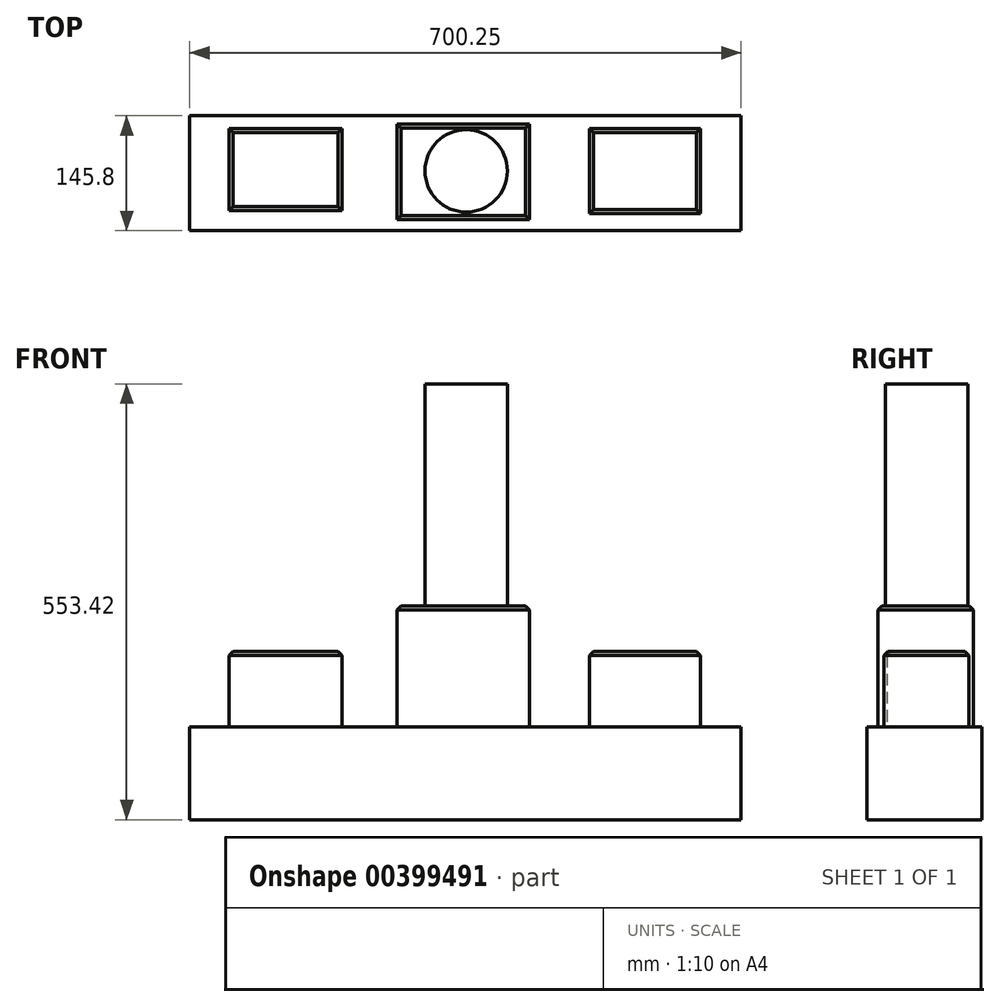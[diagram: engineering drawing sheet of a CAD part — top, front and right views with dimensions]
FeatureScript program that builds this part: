
annotation { "Feature Type Name" : "Feature", "Feature Type Description" : "" }
export const myFeature = defineFeature(function(context is Context, id is Id, definition is map)
    precondition{}
    {
        {
            var Q0;
            Q0=qCreatedBy(makeId("Front.planeOp"),FACE);
            var sketch = newSketch(context, id + "F0", { "sketchPlane" : qUnion([Q0])});
            skLineSegment(sketch, "E0.bottom", {"start": v(-52.43, 51.1) * mm, "end": v(48.89, 51.1) * mm});
            skLineSegment(sketch, "E0.top", {"start": v(-52.43, -66.7) * mm, "end": v(48.89, -66.7) * mm});
            skLineSegment(sketch, "E0.left", {"start": v(-52.43, 51.1) * mm, "end": v(-52.43, -66.7) * mm});
            skLineSegment(sketch, "E0.right", {"start": v(48.89, 51.1) * mm, "end": v(48.89, -66.7) * mm});
            skSolve(sketch);
        }
        {
            var Q0;
            Q0=makeQuery(id+"F0.imprint","IMPRINT",FACE,{"disambiguationData":[TD([[makeQuery(id+"F0.imprint","IMPRINT",EDGE,{"derivedFrom":sQuery(id+"F0.wireOp",EDGE,"E0.bottom")}),-1.0]])]});
            extrude(context, id + "F1", {"entities" : qUnion([Q0]), "depth" : 145.8 * mm});
        }
        {
            var Q0;
            Q0=makeQuery(id+"F1.opExtrude","SWEPT_FACE",FACE,{"disambiguationData":[OSD([sQuery(id+"F0.wireOp",EDGE,"E0.right")])]});
            var sketch = newSketch(context, id + "F2", { "sketchPlane" : qUnion([Q0])});
            skLineSegment(sketch, "E1.bottom", {"start": v(-145.8, 51.1) * mm, "end": v(0, 51.1) * mm});
            skLineSegment(sketch, "E1.top", {"start": v(-145.8, -66.7) * mm, "end": v(0, -66.7) * mm});
            skLineSegment(sketch, "E1.left", {"start": v(-145.8, 51.1) * mm, "end": v(-145.8, -66.7) * mm});
            skLineSegment(sketch, "E1.right", {"start": v(0, 51.1) * mm, "end": v(0, -66.7) * mm});
            skSolve(sketch);
        }
        {
            var Q0;
            Q0=makeQuery(id+"F2.imprint","IMPRINT",FACE,{"disambiguationData":[TD([[makeQuery(id+"F2.imprint","IMPRINT",EDGE,{"derivedFrom":sQuery(id+"F2.wireOp",EDGE,"E1.bottom")}),-1.0]])]});
            extrude(context, id + "F3", {"entities" : qUnion([Q0]), "operationType" : NewBodyOperationType.ADD, "depth" : 89.92 * mm});
        }
        {
            var Q0;
            Q0=makeQuery(id+"F3.boolean.opBoolean","MERGE",FACE,{"derivedFrom":[makeQuery(id+"F1.opExtrude","SWEPT_FACE",FACE,{"disambiguationData":[OSD([sQuery(id+"F0.wireOp",EDGE,"E0.bottom")])]}),makeQuery(id+"F3.opExtrude","SWEPT_FACE",FACE,{"disambiguationData":[OSD([sQuery(id+"F2.wireOp",EDGE,"E1.bottom")])]})]});
            var sketch = newSketch(context, id + "F4", { "sketchPlane" : qUnion([Q0])});
            skLineSegment(sketch, "E2.bottom", {"start": v(-43.56, -10.26) * mm, "end": v(124.66, -10.26) * mm});
            skLineSegment(sketch, "E2.top", {"start": v(-43.56, -131.8) * mm, "end": v(124.66, -131.8) * mm});
            skLineSegment(sketch, "E2.left", {"start": v(-43.56, -10.26) * mm, "end": v(-43.56, -131.8) * mm});
            skLineSegment(sketch, "E2.right", {"start": v(124.66, -10.26) * mm, "end": v(124.66, -131.8) * mm});
            skSolve(sketch);
        }
        {
            var Q0;
            Q0=makeQuery(id+"F4.imprint","IMPRINT",FACE,{"disambiguationData":[TD([[makeQuery(id+"F4.imprint","IMPRINT",EDGE,{"derivedFrom":sQuery(id+"F4.wireOp",EDGE,"E2.bottom")}),-1.0]])]});
            extrude(context, id + "F5", {"entities" : qUnion([Q0]), "operationType" : NewBodyOperationType.ADD, "depth" : 153.92 * mm});
        }
        {
            var Q0;
            Q0=makeQuery(id+"F5.opExtrude","CAP_EDGE",EDGE,{"disambiguationData":[OSD([sQuery(id+"F4.wireOp",EDGE,"E2.top")])],"isStart":false});
            var Q1;
            Q1=makeQuery(id+"F5.opExtrude","CAP_EDGE",EDGE,{"disambiguationData":[OSD([sQuery(id+"F4.wireOp",EDGE,"E2.right")])],"isStart":false});
            var Q2;
            Q2=makeQuery(id+"F5.opExtrude","CAP_EDGE",EDGE,{"disambiguationData":[OSD([sQuery(id+"F4.wireOp",EDGE,"E2.bottom")])],"isStart":false});
            var Q3;
            Q3=makeQuery(id+"F5.opExtrude","CAP_EDGE",EDGE,{"disambiguationData":[OSD([sQuery(id+"F4.wireOp",EDGE,"E2.left")])],"isStart":false});
            chamfer(context, id + "F6", {"entities" : qUnion([Q0, Q1, Q2, Q3]), "width" : 5.08 * mm, "tangentPropagation" : true});
        }
        {
            var Q0;
            Q0=makeQuery(id+"F3.opExtrude","CAP_FACE",FACE,{"disambiguationData":[OSD([sQuery(id+"F2.wireOp",EDGE,"E1.bottom"),sQuery(id+"F2.wireOp",EDGE,"E1.top"),sQuery(id+"F2.wireOp",EDGE,"E1.left"),sQuery(id+"F2.wireOp",EDGE,"E1.right")])],"isStart":false});
            var sketch = newSketch(context, id + "F7", { "sketchPlane" : qUnion([Q0])});
            skLineSegment(sketch, "E3.bottom", {"start": v(-145.8, 51.1) * mm, "end": v(0, 51.1) * mm});
            skLineSegment(sketch, "E3.top", {"start": v(-145.8, -66.7) * mm, "end": v(0, -66.7) * mm});
            skLineSegment(sketch, "E3.left", {"start": v(-145.8, 51.1) * mm, "end": v(-145.8, -66.7) * mm});
            skLineSegment(sketch, "E3.right", {"start": v(0, 51.1) * mm, "end": v(0, -66.7) * mm});
            skSolve(sketch);
        }
        {
            var Q0;
            Q0=makeQuery(id+"F7.imprint","IMPRINT",FACE,{"disambiguationData":[TD([[makeQuery(id+"F7.imprint","IMPRINT",EDGE,{"derivedFrom":sQuery(id+"F7.wireOp",EDGE,"E3.bottom")}),-1.0]])]});
            extrude(context, id + "F8", {"entities" : qUnion([Q0]), "operationType" : NewBodyOperationType.ADD, "depth" : 254.5 * mm});
        }
        {
            var Q0;
            Q0=makeQuery(id+"F1.opExtrude","SWEPT_FACE",FACE,{"disambiguationData":[OSD([sQuery(id+"F0.wireOp",EDGE,"E0.left")])]});
            var sketch = newSketch(context, id + "F9", { "sketchPlane" : qUnion([Q0])});
            skLineSegment(sketch, "E4.bottom", {"start": v(0, 51.1) * mm, "end": v(145.8, 51.1) * mm});
            skLineSegment(sketch, "E4.top", {"start": v(0, -66.7) * mm, "end": v(145.8, -66.7) * mm});
            skLineSegment(sketch, "E4.left", {"start": v(0, 51.1) * mm, "end": v(0, -66.7) * mm});
            skLineSegment(sketch, "E4.right", {"start": v(145.8, 51.1) * mm, "end": v(145.8, -66.7) * mm});
            skSolve(sketch);
        }
        {
            var Q0;
            Q0=makeQuery(id+"F9.imprint","IMPRINT",FACE,{"disambiguationData":[TD([[makeQuery(id+"F9.imprint","IMPRINT",EDGE,{"derivedFrom":sQuery(id+"F9.wireOp",EDGE,"E4.bottom")}),1.0]])]});
            extrude(context, id + "F10", {"entities" : qUnion([Q0]), "operationType" : NewBodyOperationType.ADD, "depth" : 254.5 * mm});
        }
        {
            var Q0;
            Q0=makeQuery(id+"F10.boolean.opBoolean","MERGE",FACE,{"derivedFrom":[makeQuery(id+"F8.boolean.opBoolean","MERGE",FACE,{"derivedFrom":[makeQuery(id+"F3.boolean.opBoolean","MERGE",FACE,{"derivedFrom":[makeQuery(id+"F1.opExtrude","SWEPT_FACE",FACE,{"disambiguationData":[OSD([sQuery(id+"F0.wireOp",EDGE,"E0.bottom")])]}),makeQuery(id+"F3.opExtrude","SWEPT_FACE",FACE,{"disambiguationData":[OSD([sQuery(id+"F2.wireOp",EDGE,"E1.bottom")])]})]}),makeQuery(id+"F8.opExtrude","SWEPT_FACE",FACE,{"disambiguationData":[OSD([sQuery(id+"F7.wireOp",EDGE,"E3.bottom")])]})]}),makeQuery(id+"F10.opExtrude","SWEPT_FACE",FACE,{"disambiguationData":[OSD([sQuery(id+"F9.wireOp",EDGE,"E4.bottom")])]})]});
            var sketch = newSketch(context, id + "F11", { "sketchPlane" : qUnion([Q0])});
            skLineSegment(sketch, "E5.bottom", {"start": v(341.93, -124.05) * mm, "end": v(200.74, -124.05) * mm});
            skLineSegment(sketch, "E5.top", {"start": v(341.93, -16.29) * mm, "end": v(200.74, -16.29) * mm});
            skLineSegment(sketch, "E5.left", {"start": v(341.93, -124.05) * mm, "end": v(341.93, -16.29) * mm});
            skLineSegment(sketch, "E5.right", {"start": v(200.74, -124.05) * mm, "end": v(200.74, -16.29) * mm});
            skLineSegment(sketch, "E6.bottom", {"start": v(-113.7, -120.64) * mm, "end": v(-256.92, -120.64) * mm});
            skLineSegment(sketch, "E6.top", {"start": v(-113.7, -16.29) * mm, "end": v(-256.92, -16.29) * mm});
            skLineSegment(sketch, "E6.left", {"start": v(-113.7, -120.64) * mm, "end": v(-113.7, -16.29) * mm});
            skLineSegment(sketch, "E6.right", {"start": v(-256.92, -120.64) * mm, "end": v(-256.92, -16.29) * mm});
            skSolve(sketch);
        }
        {
            var Q0;
            Q0=makeQuery(id+"F11.imprint","IMPRINT",FACE,{"disambiguationData":[TD([[makeQuery(id+"F11.imprint","IMPRINT",EDGE,{"derivedFrom":sQuery(id+"F11.wireOp",EDGE,"E6.bottom")}),-1.0]])]});
            var Q1;
            Q1=makeQuery(id+"F11.imprint","IMPRINT",FACE,{"disambiguationData":[TD([[makeQuery(id+"F11.imprint","IMPRINT",EDGE,{"derivedFrom":sQuery(id+"F11.wireOp",EDGE,"E5.bottom")}),-1.0]])]});
            extrude(context, id + "F12", {"entities" : qUnion([Q0, Q1]), "operationType" : NewBodyOperationType.ADD, "depth" : 95.76 * mm});
        }
        {
            var Q0;
            Q0=makeQuery(id+"F12.opExtrude","CAP_EDGE",EDGE,{"disambiguationData":[OSD([sQuery(id+"F11.wireOp",EDGE,"E6.top")])],"isStart":false});
            var Q1;
            Q1=makeQuery(id+"F12.opExtrude","CAP_EDGE",EDGE,{"disambiguationData":[OSD([sQuery(id+"F11.wireOp",EDGE,"E6.left")])],"isStart":false});
            var Q2;
            Q2=makeQuery(id+"F12.opExtrude","CAP_EDGE",EDGE,{"disambiguationData":[OSD([sQuery(id+"F11.wireOp",EDGE,"E6.bottom")])],"isStart":false});
            var Q3;
            Q3=makeQuery(id+"F12.opExtrude","CAP_EDGE",EDGE,{"disambiguationData":[OSD([sQuery(id+"F11.wireOp",EDGE,"E6.right")])],"isStart":false});
            var Q4;
            Q4=makeQuery(id+"F12.opExtrude","CAP_EDGE",EDGE,{"disambiguationData":[OSD([sQuery(id+"F11.wireOp",EDGE,"E5.top")])],"isStart":false});
            var Q5;
            Q5=makeQuery(id+"F12.opExtrude","CAP_EDGE",EDGE,{"disambiguationData":[OSD([sQuery(id+"F11.wireOp",EDGE,"E5.right")])],"isStart":false});
            var Q6;
            Q6=makeQuery(id+"F12.opExtrude","CAP_EDGE",EDGE,{"disambiguationData":[OSD([sQuery(id+"F11.wireOp",EDGE,"E5.left")])],"isStart":false});
            var Q7;
            Q7=makeQuery(id+"F12.opExtrude","CAP_EDGE",EDGE,{"disambiguationData":[OSD([sQuery(id+"F11.wireOp",EDGE,"E5.bottom")])],"isStart":false});
            chamfer(context, id + "F13", {"entities" : qUnion([Q0, Q1, Q2, Q3, Q4, Q5, Q6, Q7]), "width" : 5.08 * mm, "tangentPropagation" : true});
        }
        {
            var Q0;
            Q0=makeQuery(id+"F5.opExtrude","CAP_FACE",FACE,{"disambiguationData":[OSD([sQuery(id+"F4.wireOp",EDGE,"E2.bottom"),sQuery(id+"F4.wireOp",EDGE,"E2.top"),sQuery(id+"F4.wireOp",EDGE,"E2.left"),sQuery(id+"F4.wireOp",EDGE,"E2.right")])],"isStart":false});
            var sketch = newSketch(context, id + "F14", { "sketchPlane" : qUnion([Q0])});
            skCircle(sketch, "E7", {"center": v(44.2, -70.02) * mm, "radius": 52.27 * mm});
            skSolve(sketch);
        }
        {
            var Q0;
            Q0 = qSketchRegion(id + "F14", true);
            extrude(context, id + "F15", {"entities" : qUnion([Q0]), "operationType" : NewBodyOperationType.ADD, "depth" : 281.7 * mm});
        }
    });
